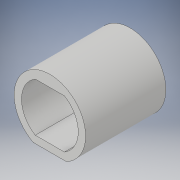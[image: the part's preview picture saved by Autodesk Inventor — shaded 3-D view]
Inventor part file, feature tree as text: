
AUTODESK INVENTOR PART (.ipt)
format: ipt  version: 2017 (Build 210142000, 142)  size: 104,448 bytes
history: native  units: in
note: dims shown in document units (in); Inventor stores cm internally (conversion verified against a paired STEP export)
features: other x1, sketch x1
ambient origin geometry x8: Origin, YZ Plane, XZ Plane, XY Plane, X Axis, Y Axis, Z Axis, Center Point
bodies: Solid1 (feature_tree)
feature tree (2):
  other  "corridor"
  sketch  "Sketch1"  dims[d0=6.6667in d1=4.0in d2=1.0in d3=11.0in d4=0.0in d7=1.0in d20=1.0in d21=4.8944in]
